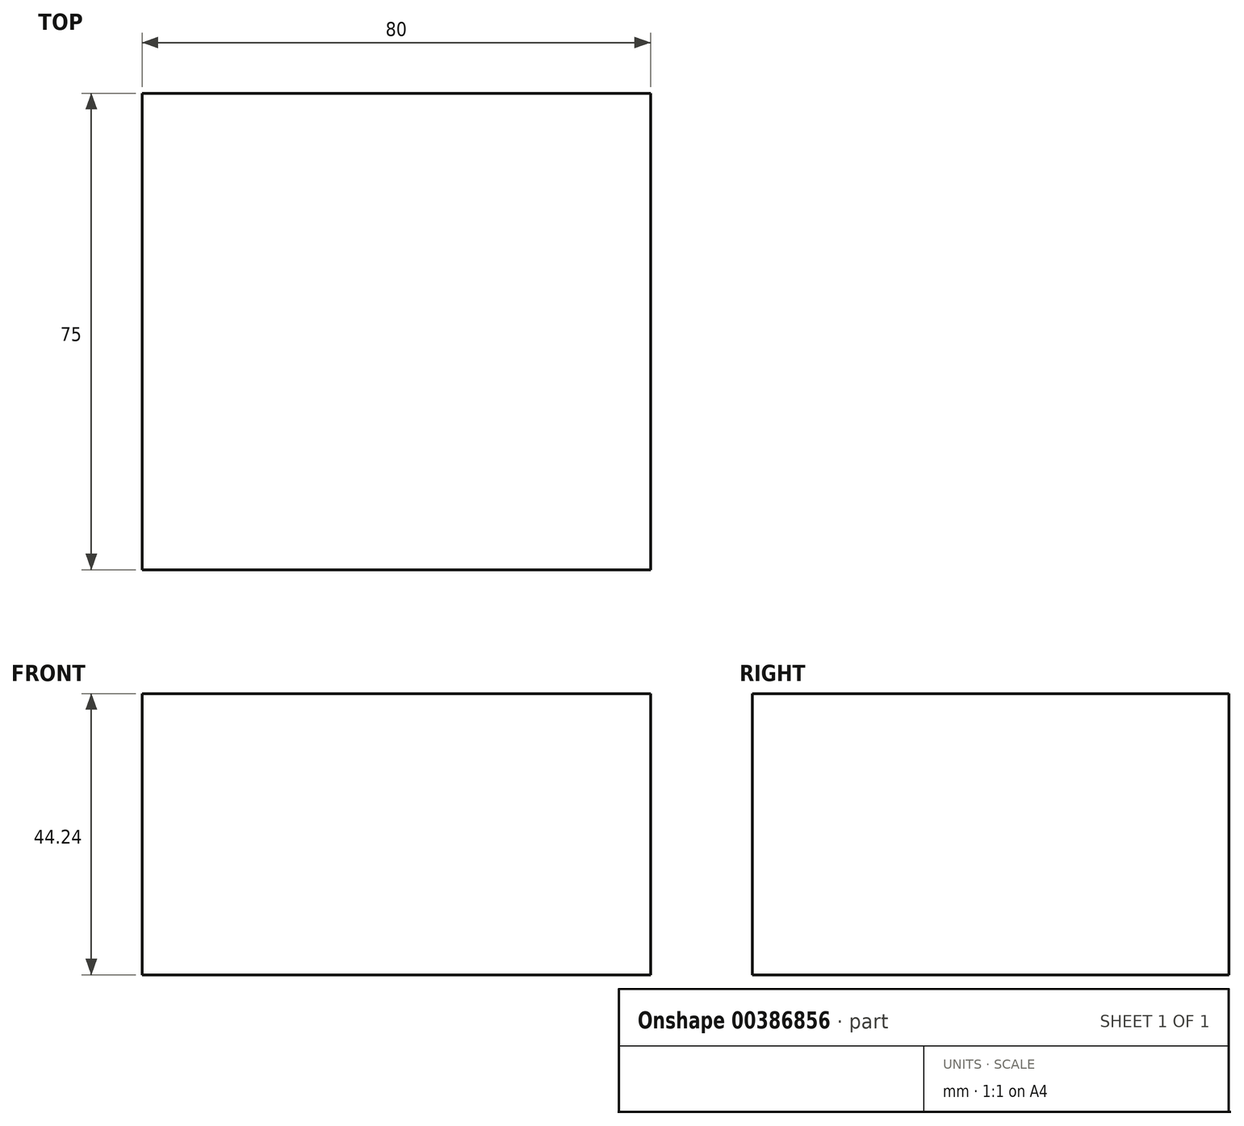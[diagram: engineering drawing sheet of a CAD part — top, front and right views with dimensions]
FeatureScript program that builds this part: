
annotation { "Feature Type Name" : "Feature", "Feature Type Description" : "" }
export const myFeature = defineFeature(function(context is Context, id is Id, definition is map)
    precondition{}
    {
        {
            var Q0;
            Q0=qCreatedBy(makeId("Front.planeOp"),FACE);
            var sketch = newSketch(context, id + "F0", { "sketchPlane" : qUnion([Q0])});
            skLineSegment(sketch, "E0.bottom", {"start": v(-40, 22.12) * mm, "end": v(40, 22.12) * mm});
            skLineSegment(sketch, "E0.top", {"start": v(-40, -22.12) * mm, "end": v(40, -22.12) * mm});
            skLineSegment(sketch, "E0.left", {"start": v(-40, 22.12) * mm, "end": v(-40, -22.12) * mm});
            skLineSegment(sketch, "E0.right", {"start": v(40, 22.12) * mm, "end": v(40, -22.12) * mm});
            skPoint(sketch, "E0.middle", {"position": v(0, 0) * mm});
            skSolve(sketch);
        }
        {
            var Q0;
            Q0=makeQuery(id+"F0.imprint","IMPRINT",FACE,{"disambiguationData":[TD([[makeQuery(id+"F0.imprint","IMPRINT",EDGE,{"derivedFrom":sQuery(id+"F0.wireOp",EDGE,"E0.bottom")}),-1.0]])]});
            extrude(context, id + "F1", {"entities" : qUnion([Q0]), "depth" : 75 * mm});
        }
    });
